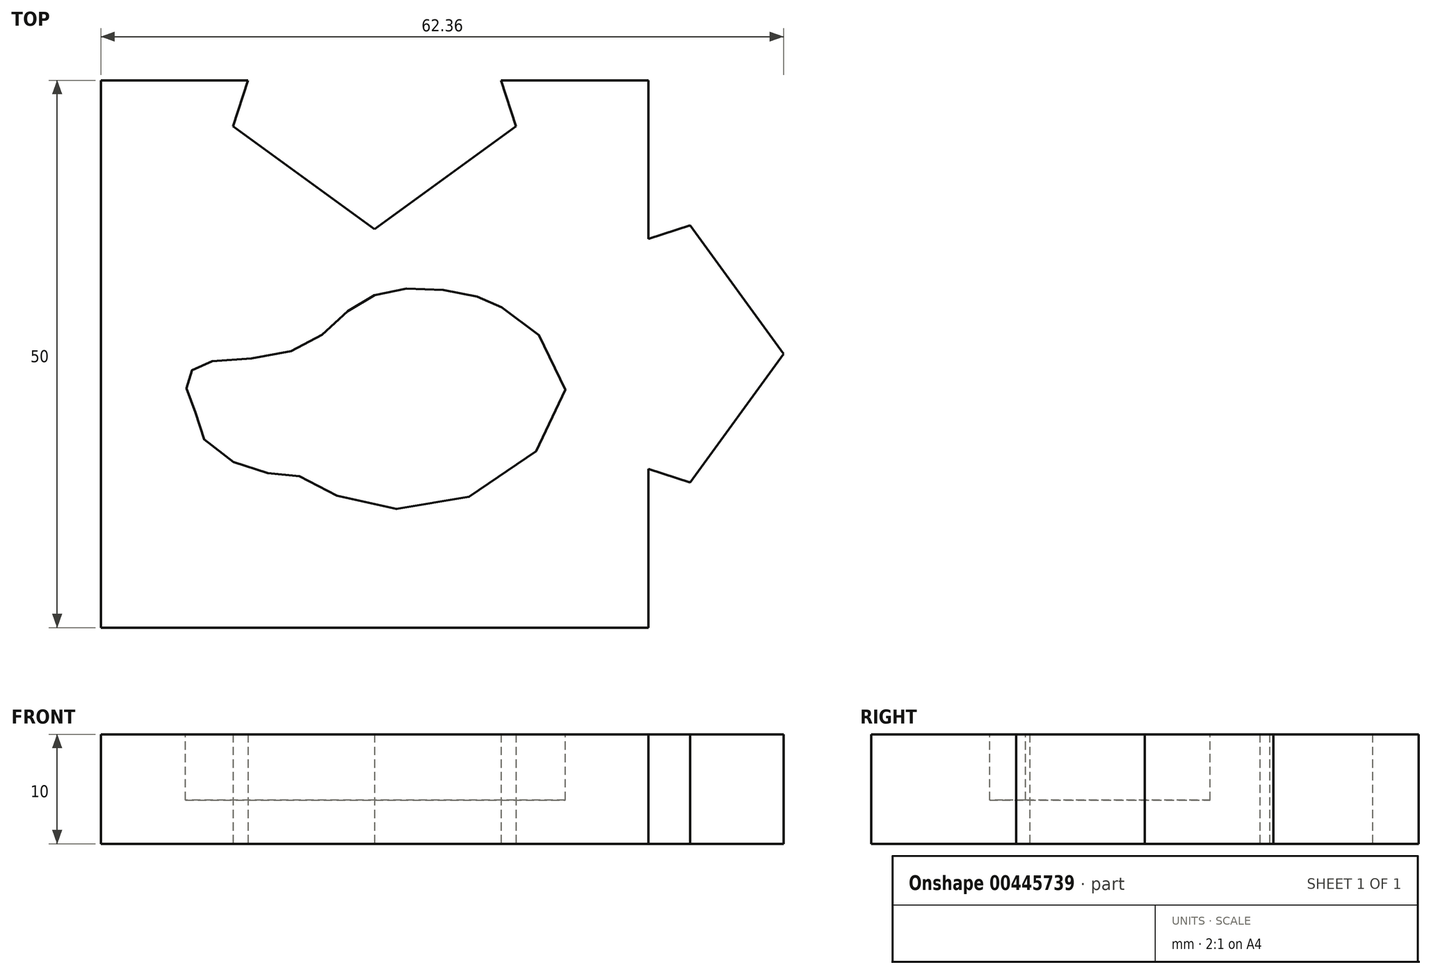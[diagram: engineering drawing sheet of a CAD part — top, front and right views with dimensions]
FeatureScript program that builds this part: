
annotation { "Feature Type Name" : "Feature", "Feature Type Description" : "" }
export const myFeature = defineFeature(function(context is Context, id is Id, definition is map)
    precondition{}
    {
        {
            var Q0;
            Q0=qCreatedBy(makeId("Top.planeOp"),FACE);
            var sketch = newSketch(context, id + "F0", { "sketchPlane" : qUnion([Q0])});
            skLineSegment(sketch, "E0.bottom", {"start": v(25, -25) * mm, "end": v(-25, -25) * mm});
            skLineSegment(sketch, "E0.top", {"start": v(25, 25) * mm, "end": v(-25, 25) * mm});
            skLineSegment(sketch, "E0.left", {"start": v(25, -25) * mm, "end": v(25, 25) * mm});
            skLineSegment(sketch, "E0.right", {"start": v(-25, -25) * mm, "end": v(-25, 25) * mm});
            skPoint(sketch, "E0.middle", {"position": v(0, 0) * mm});
            skLineSegment(sketch, "E1", {"start": v(25, 25) * mm, "end": v(15, 25) * mm, "construction": true});
            skLineSegment(sketch, "E2", {"start": v(15, 25) * mm, "end": v(15, -25) * mm, "construction": true});
            skCircle(sketch, "E3.cCircle", {"center": v(25, 0) * mm, "radius": 10 * mm, "construction": true});
            skLineSegment(sketch, "E3.0", {"start": v(15, -7.27) * mm, "end": v(15, 7.27) * mm});
            skLineSegment(sketch, "E3.1", {"start": v(15, 7.27) * mm, "end": v(28.82, 11.76) * mm});
            skLineSegment(sketch, "E3.2", {"start": v(28.82, 11.76) * mm, "end": v(37.36, 0) * mm});
            skLineSegment(sketch, "E3.3", {"start": v(37.36, 0) * mm, "end": v(28.82, -11.76) * mm});
            skLineSegment(sketch, "E3.4", {"start": v(28.82, -11.76) * mm, "end": v(15, -7.27) * mm});
            skPoint(sketch, "E3.0.midPoint", {"position": v(15, 0) * mm});
            skLineSegment(sketch, "E4", {"start": v(-25, 25) * mm, "end": v(-25, 36) * mm, "construction": true});
            skLineSegment(sketch, "E5", {"start": v(-25, 36) * mm, "end": v(25, 36) * mm, "construction": true});
            skCircle(sketch, "E6.cCircle", {"center": v(0, 25) * mm, "radius": 11 * mm, "construction": true});
            skLineSegment(sketch, "E6.0", {"start": v(-8, 36) * mm, "end": v(8, 36) * mm});
            skLineSegment(sketch, "E6.1", {"start": v(8, 36) * mm, "end": v(12.93, 20.8) * mm});
            skLineSegment(sketch, "E6.2", {"start": v(12.93, 20.8) * mm, "end": v(0, 11.4) * mm});
            skLineSegment(sketch, "E6.3", {"start": v(0, 11.4) * mm, "end": v(-12.93, 20.8) * mm});
            skLineSegment(sketch, "E6.4", {"start": v(-12.93, 20.8) * mm, "end": v(-8, 36) * mm});
            skPoint(sketch, "E6.0.midPoint", {"position": v(0, 36) * mm});
            skSolve(sketch);
        }
        {
            var Q0;
            {var subQ10=sQuery(id+"F0.wireOp",EDGE,"E0.bottom");Q0=makeQuery(id+"F0.imprint","IMPRINT",FACE,{"disambiguationData":[TD([[makeQuery(id+"F0.imprint","IMPRINT",EDGE,{"derivedFrom":subQ10}),-1.0]])]});}
            var Q1;
            {var subQ1=sQuery(id+"F0.wireOp",EDGE,"E3.2");Q1=makeQuery(id+"F0.imprint","IMPRINT",FACE,{"disambiguationData":[TD([[makeQuery(id+"F0.imprint","IMPRINT",EDGE,{"derivedFrom":subQ1}),-1.0]])]});}
            var Q2;
            {var subQ5=sQuery(id+"F0.wireOp",EDGE,"E3.0");Q2=makeQuery(id+"F0.imprint","IMPRINT",FACE,{"disambiguationData":[TD([[makeQuery(id+"F0.imprint","IMPRINT",EDGE,{"derivedFrom":subQ5}),-1.0]])]});}
            extrude(context, id + "F1", {"entities" : qUnion([Q0, Q1, Q2]), "depth" : 10 * mm});
        }
        {
            var Q0;
            Q0=makeQuery(id+"F1.opExtrude","CAP_FACE",FACE,{"disambiguationData":[OSD([sQuery(id+"F0.wireOp",EDGE,"E0.bottom"),sQuery(id+"F0.wireOp",EDGE,"E0.top"),sQuery(id+"F0.wireOp",EDGE,"E0.left"),sQuery(id+"F0.wireOp",EDGE,"E0.right"),sQuery(id+"F0.wireOp",EDGE,"E3.1"),sQuery(id+"F0.wireOp",EDGE,"E3.2"),sQuery(id+"F0.wireOp",EDGE,"E3.3"),sQuery(id+"F0.wireOp",EDGE,"E3.4"),sQuery(id+"F0.wireOp",EDGE,"E6.1"),sQuery(id+"F0.wireOp",EDGE,"E6.2"),sQuery(id+"F0.wireOp",EDGE,"E6.3"),sQuery(id+"F0.wireOp",EDGE,"E6.4")])],"isStart":false});
            var sketch = newSketch(context, id + "F2", { "sketchPlane" : qUnion([Q0])});
            skFitSpline(sketch, "E7", {"points": [v(-3.42, -12.95) * mm, v(8, -13.3) * mm, v(17.43, -3.32) * mm, v(12.68, 3.69) * mm, v(10.47, 4.72) * mm, v(8.44, 5.56) * mm, v(4.8, 5.92) * mm, v(1.62, 5.85) * mm, v(-0.97, 4.9) * mm, v(-3.05, 3.4) * mm, v(-5.6, 1.13) * mm, v(-8.78, 0) * mm, v(-13.3, -0.62) * mm, v(-16, -0.86) * mm, v(-16.7, -1.51) * mm, v(-17.26, -2.45) * mm, v(-17, -3.58) * mm, v(-16.37, -5.35) * mm, v(-15.9, -7.3) * mm, v(-13.45, -9.55) * mm, v(-10.1, -10.87) * mm, v(-7.41, -11.01) * mm, v(-3.42, -12.95) * mm]});
            skSolve(sketch);
        }
        {
            var Q0;
            Q0=makeQuery(id+"F2.imprint","IMPRINT",FACE,{"disambiguationData":[TD([[makeQuery(id+"F2.imprint","IMPRINT",EDGE,{"derivedFrom":sQuery(id+"F2.wireOp",EDGE,"E7")}),1.0]])]});
            extrude(context, id + "F3", {"entities" : qUnion([Q0]), "operationType" : NewBodyOperationType.REMOVE, "oppositeDirection" : true, "depth" : 6 * mm});
        }
    });
